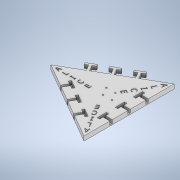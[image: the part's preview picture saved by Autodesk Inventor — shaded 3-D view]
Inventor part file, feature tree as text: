
AUTODESK INVENTOR PART (.ipt)
format: ipt  version: 2022.3 (Build 263350000, 350)  size: 705,024 bytes
history: native  units: mm
features: extrude x6, thicken_offset x6, sketch x5, hole x1, emboss x1, pattern_circular x1, projected_geometry x1
ambient origin geometry x8: Origin, YZ Plane, XZ Plane, XY Plane, X Axis, Y Axis, Z Axis, Center Point
bodies: Solid1 (feature_tree)
feature tree (21):
  sketch  "Sketch1"  dims[d1=200.0mm d2=35.0mm]
  extrude  "Extrusion1"  Depth=35.0mm
  extrude  "Extrusion2"  Depth=5.0mm
  extrude  "Extrusion3"  Depth=30.0mm
  extrude  "Extrusion4"  Depth=10.0mm TaperAngle=0.0deg
  sketch  "Sketch3"  dims[d5=20.0mm d6=30.0mm d8=40.0mm d9=30.0mm d11=40.0mm]
  extrude  "Extrusion6"  Depth=10.0mm
  extrude  "Extrusion7"  Depth=10.0mm
  hole  "Hole1"  [1 undecoded]
  thicken_offset  "Thicken1"
  thicken_offset  "Thicken2"
  thicken_offset  "Thicken3"
  thicken_offset  "Thicken4"
  thicken_offset  "Thicken5"
  thicken_offset  "Thicken6"
  emboss  "Emboss1"
  pattern_circular  "Circular Pattern1"  [2 undecoded]
  sketch  "Sketch2"  dims[d3=5.0mm d4=5.0mm]
  projected_geometry  "Projected Loop1"
  sketch  "Sketch4"  dims[d14=10.0mm d15=0.0mm d16=10.0mm d17=0.0mm]
  sketch  "Sketch5"  dims[d18=2.2mm d19=0.0mm d20=22.0mm d21=3.0mm d22=1.5mm d23=0.0mm d24=15.0mm d25=120.0deg d26=10.0mm d27=5.0mm d28=20.0mm d29=90.0deg d30=5.0mm d31=2.5mm d32=5.0mm d33=20.0mm d35=120.0deg d37=30.0mm d39=40.0mm d40=30.0mm d42=40.0mm d45=30.0mm d47=40.0mm d48=30.0mm d50=40.0mm d55=7.8mm d56=0.0mm d57=10.0mm d58=0.0mm d59=40.0mm d60=2.2mm d61=6.0mm d62=3.1mm d63=4.1mm d64=90.0deg d65=2.2mm d66=0.0mm d67=0.2mm d68=0.05mm d69=0.2mm d70=0.05mm d71=0.2mm d72=0.05mm d73=0.2mm d74=0.05mm d75=0.2mm d76=0.05mm d77=0.2mm d78=0.05mm d79=1.0mm d80=0.0mm d81=30.0mm d82=360.0deg d84=16.0mm d85=2.0mm d86=0.0mm d87=8.0mm d88=10.0mm d89=50.0mm d90=50.0mm d91=50.0mm d92=50.0mm d93=90.0deg d94=50.0mm d95=50.0mm]
note: 3 required parameter values undecoded (feature->parameter linkage not recoverable at this tier; creation-order binding heuristic only, values carry confidence <= 0.55)
